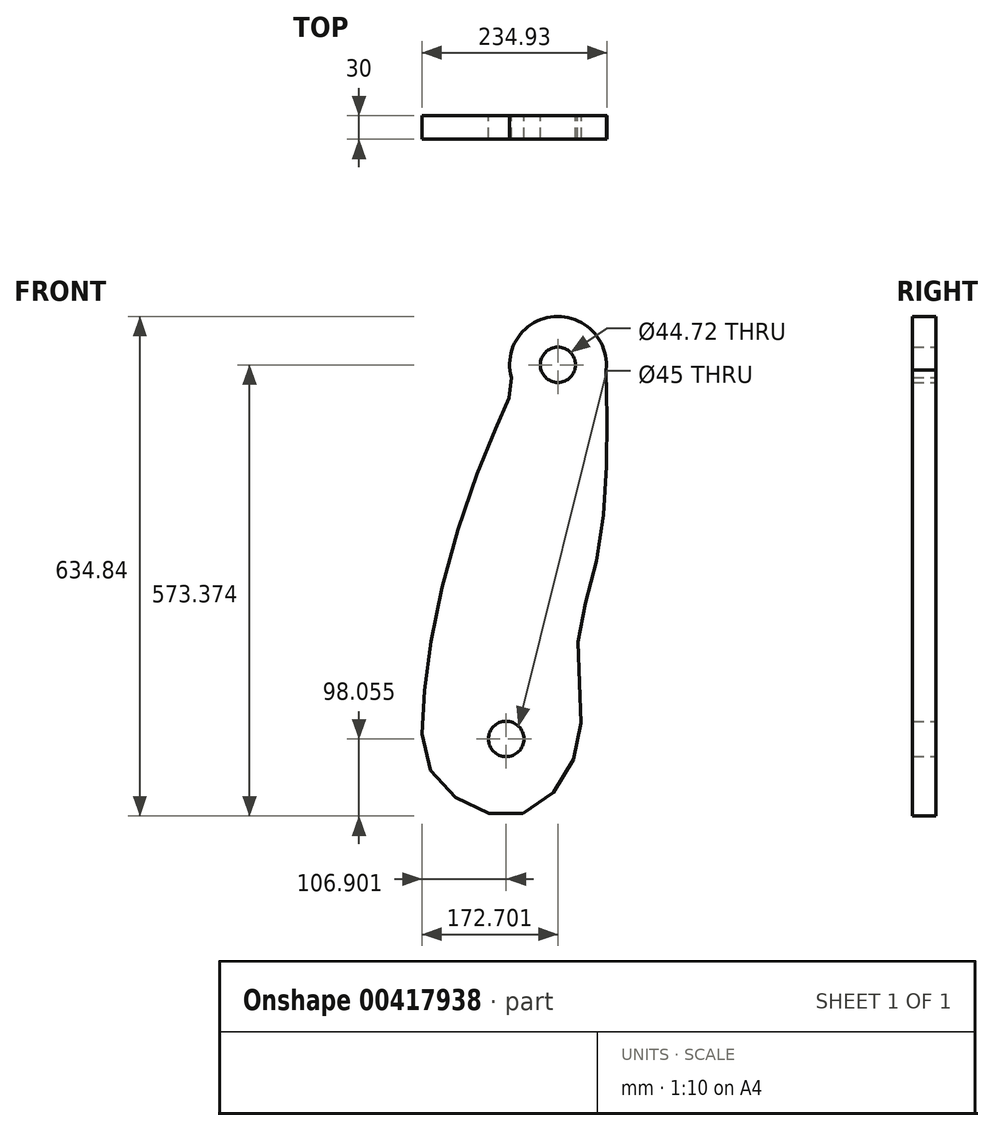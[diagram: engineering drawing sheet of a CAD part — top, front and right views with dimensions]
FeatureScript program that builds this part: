
annotation { "Feature Type Name" : "Feature", "Feature Type Description" : "" }
export const myFeature = defineFeature(function(context is Context, id is Id, definition is map)
    precondition{}
    {
        {
            var Q0;
            Q0=qCreatedBy(makeId("Front.planeOp"),FACE);
            var sketch = newSketch(context, id + "F0", { "sketchPlane" : qUnion([Q0])});
            skArc(sketch, "E0", {"start": v(6.04, 12.15) * mm, "mid": v(1.63, 16.66) * mm, "end": v(-2, 11.5) * mm});
            skFitSpline(sketch, "E1", {"points": [v(-2, 11.5) * mm, v(-2.1, 10.04) * mm, v(-4, 5.57) * mm, v(-7.8, -6.05) * mm, v(-9.42, -15.8) * mm, v(-8.92, -21.58) * mm, v(-5.24, -24.92) * mm, v(-0.96, -25.42) * mm, v(2.83, -21.86) * mm, v(3.94, -16.85) * mm, v(3.66, -10.78) * mm, v(5.1, -4.66) * mm, v(6.05, 3.58) * mm, v(6.04, 12.15) * mm], "startDerivative": vector(1.24, -35.43) * mm, "endDerivative": vector(-2, 93.42) * mm});
            skCircle(sketch, "E2", {"center": v(1.96, 12.57) * mm, "radius": 1.5 * mm});
            skCircle(sketch, "E3", {"center": v(-2.43, -19.12) * mm, "radius": 1.5 * mm});
            skSolve(sketch);
        }
        {
            var Q0;
            Q0=qSketchRegion(id+"F0",true);
            extrude(context, id + "F1", {"entities" : qUnion([Q0]), "depth" : 2 * mm, "offsetDistance" : 25 * mm});
        }
        {
            var Q0;
            Q0=makeQuery(id+"F1.opExtrude","SWEPT_BODY",BODY,{"disambiguationData":[OSD([sQuery(id+"F0.wireOp",EDGE,"E0"),sQuery(id+"F0.wireOp",EDGE,"E1"),sQuery(id+"F0.wireOp",EDGE,"E2"),sQuery(id+"F0.wireOp",EDGE,"E3")])]});
            var Q1;
            Q1=qCreatedBy(makeId("Origin.pointOp"),VERTEX);
            transform(context, id + "F2", {"entities" : qUnion([Q0]), "transformType" : TransformType.SCALE_UNIFORMLY, "scale" : 10, "scalePoint" : qUnion([Q1]), "makeCopy" : false});
        }
        {
            var Q0;
            Q0=makeQuery(id+"F1.opExtrude","SWEPT_BODY",BODY,{"disambiguationData":[OSD([sQuery(id+"F0.wireOp",EDGE,"E0"),sQuery(id+"F0.wireOp",EDGE,"E1"),sQuery(id+"F0.wireOp",EDGE,"E2"),sQuery(id+"F0.wireOp",EDGE,"E3")])]});
            var Q1;
            Q1=qCreatedBy(makeId("Origin.pointOp"),VERTEX);
            transform(context, id + "F3", {"entities" : qUnion([Q0]), "transformType" : TransformType.SCALE_UNIFORMLY, "scale" : 1.5, "scalePoint" : qUnion([Q1]), "makeCopy" : false});
        }
    });
